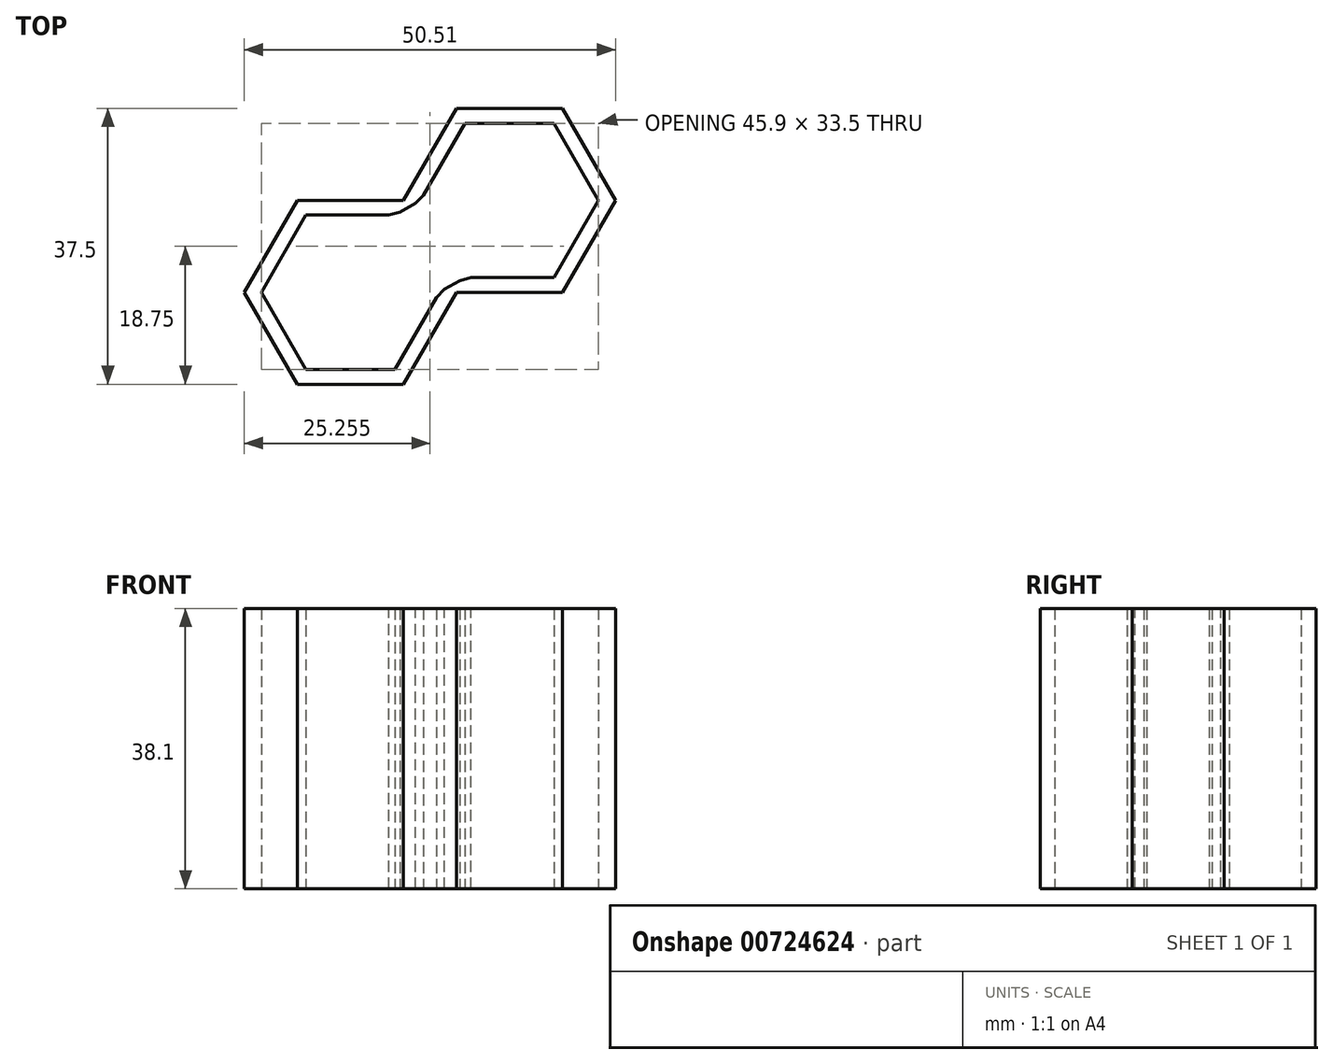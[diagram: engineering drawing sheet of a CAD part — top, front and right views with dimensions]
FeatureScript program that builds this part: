
annotation { "Feature Type Name" : "Feature", "Feature Type Description" : "" }
export const myFeature = defineFeature(function(context is Context, id is Id, definition is map)
    precondition{}
    {
        {
            var Q0;
            Q0=qCreatedBy(makeId("Top.planeOp"),FACE);
            var sketch = newSketch(context, id + "F0", { "sketchPlane" : qUnion([Q0])});
            skCircle(sketch, "E0.cCircle", {"center": v(0, 0) * mm, "radius": 10.5 * mm, "construction": true});
            skLineSegment(sketch, "E0.0", {"start": v(6.06, -10.5) * mm, "end": v(-6.06, -10.5) * mm});
            skLineSegment(sketch, "E0.1", {"start": v(-6.06, -10.5) * mm, "end": v(-12.12, 0) * mm});
            skLineSegment(sketch, "E0.2", {"start": v(-12.12, 0) * mm, "end": v(-6.06, 10.5) * mm});
            skLineSegment(sketch, "E0.3", {"start": v(-6.06, 10.5) * mm, "end": v(6.06, 10.5) * mm});
            skLineSegment(sketch, "E0.5", {"start": v(12.12, 0) * mm, "end": v(6.06, -10.5) * mm});
            skPoint(sketch, "E0.0.midPoint", {"position": v(0, -10.5) * mm});
            skCircle(sketch, "E1.cCircle", {"center": v(0, 0) * mm, "radius": 12.5 * mm, "construction": true});
            skLineSegment(sketch, "E1.0", {"start": v(7.22, -12.5) * mm, "end": v(-7.22, -12.5) * mm});
            skLineSegment(sketch, "E1.1", {"start": v(-7.22, -12.5) * mm, "end": v(-14.43, 0) * mm});
            skLineSegment(sketch, "E1.2", {"start": v(-14.43, 0) * mm, "end": v(-7.22, 12.5) * mm});
            skLineSegment(sketch, "E1.3", {"start": v(-7.22, 12.5) * mm, "end": v(7.22, 12.5) * mm});
            skLineSegment(sketch, "E1.5", {"start": v(14.43, 0) * mm, "end": v(7.22, -12.5) * mm});
            skPoint(sketch, "E1.0.midPoint", {"position": v(0, -12.5) * mm});
            skCircle(sketch, "E2.cCircle", {"center": v(21.65, 12.5) * mm, "radius": 10.5 * mm, "construction": true});
            skLineSegment(sketch, "E2.0", {"start": v(27.71, 2) * mm, "end": v(15.59, 2) * mm});
            skLineSegment(sketch, "E2.2", {"start": v(9.53, 12.5) * mm, "end": v(15.59, 23) * mm});
            skLineSegment(sketch, "E2.3", {"start": v(15.59, 23) * mm, "end": v(27.71, 23) * mm});
            skLineSegment(sketch, "E2.4", {"start": v(27.71, 23) * mm, "end": v(33.77, 12.5) * mm});
            skLineSegment(sketch, "E2.5", {"start": v(33.77, 12.5) * mm, "end": v(27.71, 2) * mm});
            skPoint(sketch, "E2.0.midPoint", {"position": v(21.65, 2) * mm});
            skCircle(sketch, "E3.cCircle", {"center": v(21.65, 12.5) * mm, "radius": 12.5 * mm, "construction": true});
            skLineSegment(sketch, "E3.0", {"start": v(28.87, 0) * mm, "end": v(14.43, 0) * mm});
            skLineSegment(sketch, "E3.2", {"start": v(7.22, 12.5) * mm, "end": v(14.43, 25) * mm});
            skLineSegment(sketch, "E3.3", {"start": v(14.43, 25) * mm, "end": v(28.87, 25) * mm});
            skLineSegment(sketch, "E3.4", {"start": v(28.87, 25) * mm, "end": v(36.08, 12.5) * mm});
            skLineSegment(sketch, "E3.5", {"start": v(36.08, 12.5) * mm, "end": v(28.87, 0) * mm});
            skPoint(sketch, "E3.0.midPoint", {"position": v(21.65, 0) * mm});
            skLineSegment(sketch, "E4", {"start": v(9.53, 12.5) * mm, "end": v(6.06, 10.5) * mm});
            skLineSegment(sketch, "E5", {"start": v(12.12, 0) * mm, "end": v(15.59, 2) * mm});
            skSolve(sketch);
        }
        {
            var Q0;
            Q0=makeQuery(id+"F0.imprint","IMPRINT",FACE,{"disambiguationData":[TD([[makeQuery(id+"F0.imprint","IMPRINT",EDGE,{"derivedFrom":sQuery(id+"F0.wireOp",EDGE,"E0.0")}),1.0]])]});
            extrude(context, id + "F1", {"entities" : qUnion([Q0]), "depth" : 38.1 * mm, "offsetDistance" : 25 * mm});
        }
        {
            var Q0;
            Q0=makeQuery(id+"F1.opExtrude","SWEPT_EDGE",EDGE,{"disambiguationData":[OSD([sQuery(id+"F0.wireOp",EDGE,"E0.3"),sQuery(id+"F0.wireOp",EDGE,"E4")])]});
            var Q1;
            Q1=makeQuery(id+"F1.opExtrude","SWEPT_EDGE",EDGE,{"disambiguationData":[OSD([sQuery(id+"F0.wireOp",EDGE,"E2.2"),sQuery(id+"F0.wireOp",EDGE,"E4")])]});
            var Q2;
            Q2=makeQuery(id+"F1.opExtrude","SWEPT_EDGE",EDGE,{"disambiguationData":[OSD([sQuery(id+"F0.wireOp",EDGE,"E0.5"),sQuery(id+"F0.wireOp",EDGE,"E5")])]});
            var Q3;
            Q3=makeQuery(id+"F1.opExtrude","SWEPT_EDGE",EDGE,{"disambiguationData":[OSD([sQuery(id+"F0.wireOp",EDGE,"E2.0"),sQuery(id+"F0.wireOp",EDGE,"E5")])]});
            chamfer(context, id + "F2", {"entities" : qUnion([Q0, Q1, Q2, Q3]), "width" : 3 * mm, "tangentPropagation" : true});
        }
    });
